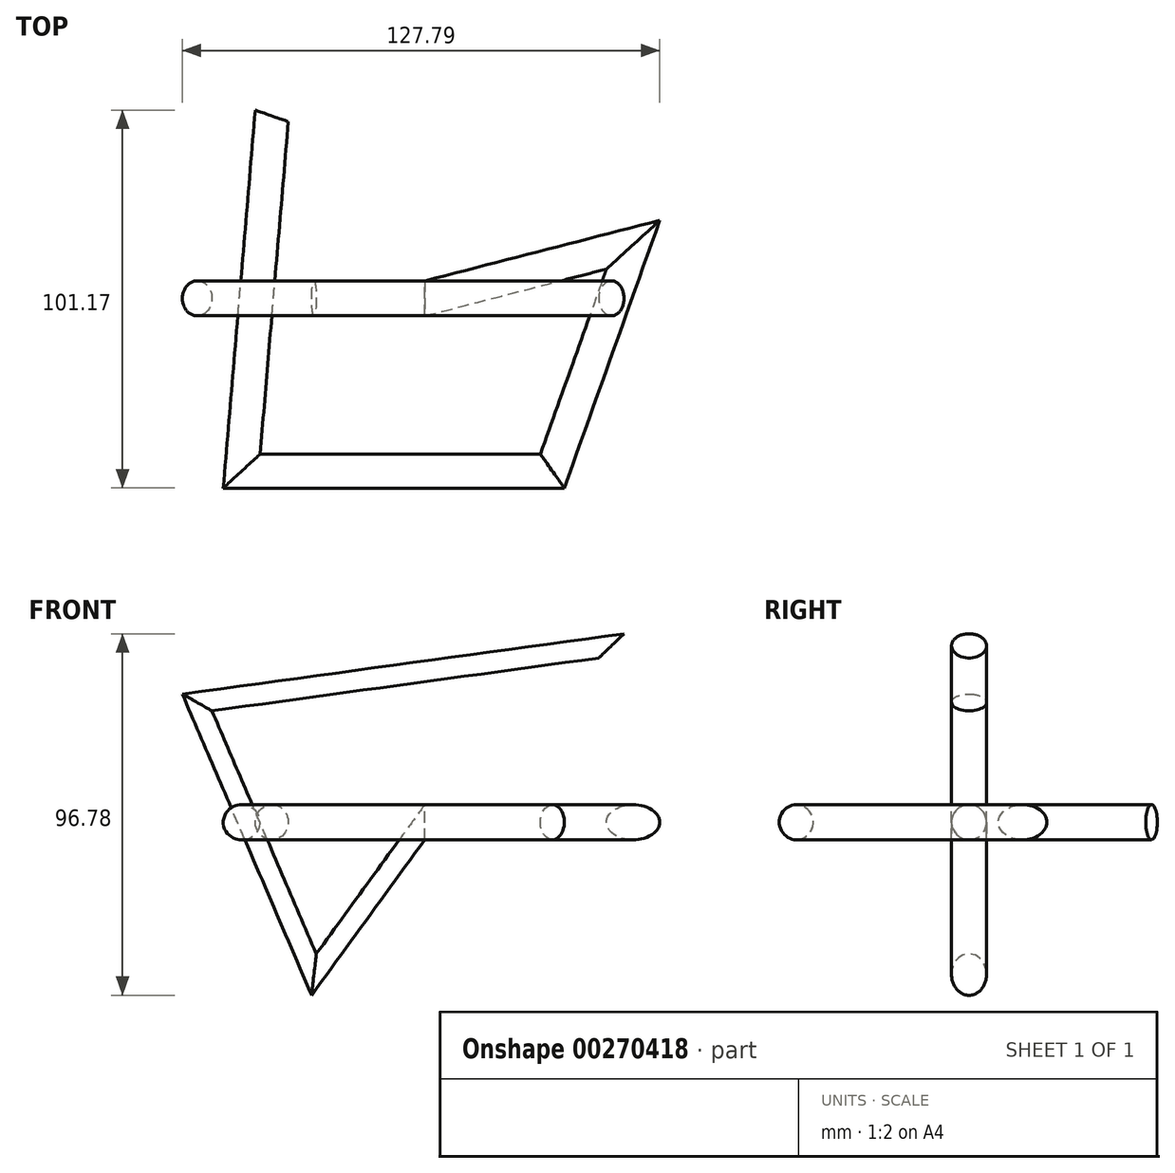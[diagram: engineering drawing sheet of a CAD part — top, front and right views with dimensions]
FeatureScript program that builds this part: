
annotation { "Feature Type Name" : "Feature", "Feature Type Description" : "" }
export const myFeature = defineFeature(function(context is Context, id is Id, definition is map)
    precondition{}
    {
        {
            var Q0;
            Q0=qCreatedBy(makeId("Top.planeOp"),FACE);
            var sketch = newSketch(context, id + "F0", { "sketchPlane" : qUnion([Q0])});
            skLineSegment(sketch, "E0", {"start": v(-40.94, 48.83) * mm, "end": v(-49, -46.26) * mm});
            skLineSegment(sketch, "E1", {"start": v(-49, -46.26) * mm, "end": v(34.17, -46.26) * mm});
            skLineSegment(sketch, "E2", {"start": v(34.17, -46.26) * mm, "end": v(55.76, 14.34) * mm});
            skLineSegment(sketch, "E3", {"start": v(55.76, 14.34) * mm, "end": v(0, 0) * mm});
            skSolve(sketch);
        }
        {
            var Q0;
            Q0=qCreatedBy(makeId("Front.planeOp"),FACE);
            var sketch = newSketch(context, id + "F1", { "sketchPlane" : qUnion([Q0])});
            skLineSegment(sketch, "E4", {"start": v(0, 0) * mm, "end": v(-29.65, -40.78) * mm});
            skLineSegment(sketch, "E5", {"start": v(-29.65, -40.78) * mm, "end": v(-60.92, 32.07) * mm});
            skLineSegment(sketch, "E6", {"start": v(-60.92, 32.07) * mm, "end": v(49.96, 47.22) * mm});
            skLineSegment(sketch, "E7", {"start": v(49.96, 47.22) * mm, "end": v(49.96, -51.1) * mm});
            skSolve(sketch);
        }
        {
            var Q0;
            Q0=qCreatedBy(makeId("Right.planeOp"),FACE);
            var sketch = newSketch(context, id + "F2", { "sketchPlane" : qUnion([Q0])});
            skCircle(sketch, "E8", {"center": v(0, 0) * mm, "radius": 4.68 * mm});
            skSolve(sketch);
        }
        {
            var Q0;
            Q0=makeQuery(id+"F2.imprint","IMPRINT",FACE,{"disambiguationData":[TD([[makeQuery(id+"F2.imprint","IMPRINT",EDGE,{"derivedFrom":sQuery(id+"F2.wireOp",EDGE,"E8")}),1.0]])]});
            var Q1;
            Q1=sQuery(id+"F1.wireOp",EDGE,"E4");
            var Q2;
            Q2=sQuery(id+"F1.wireOp",EDGE,"E5");
            var Q3;
            Q3=sQuery(id+"F1.wireOp",EDGE,"E6");
            sweep(context, id + "F3", {"profiles" : qUnion([Q0]), "path" : qUnion([Q1, Q2, Q3])});
        }
        {
            var Q0;
            Q0=makeQuery(id+"F2.imprint","IMPRINT",FACE,{"disambiguationData":[TD([[makeQuery(id+"F2.imprint","IMPRINT",EDGE,{"derivedFrom":sQuery(id+"F2.wireOp",EDGE,"E8")}),1.0]])]});
            var Q1;
            Q1=sQuery(id+"F0.wireOp",EDGE,"E3");
            var Q2;
            Q2=sQuery(id+"F0.wireOp",EDGE,"E2");
            var Q3;
            Q3=sQuery(id+"F0.wireOp",EDGE,"E1");
            var Q4;
            Q4=sQuery(id+"F0.wireOp",EDGE,"E0");
            sweep(context, id + "F4", {"profiles" : qUnion([Q0]), "path" : qUnion([Q1, Q2, Q3, Q4])});
        }
    });
